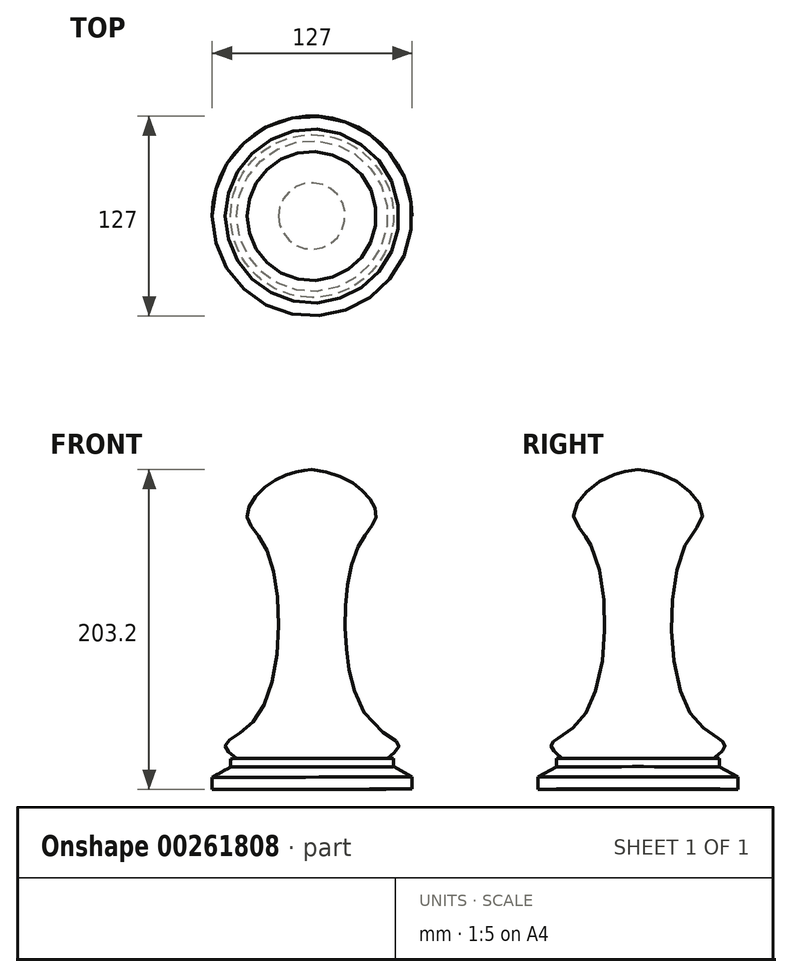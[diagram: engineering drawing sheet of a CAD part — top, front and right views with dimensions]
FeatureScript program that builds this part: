
annotation { "Feature Type Name" : "Feature", "Feature Type Description" : "" }
export const myFeature = defineFeature(function(context is Context, id is Id, definition is map)
    precondition{}
    {
        {
            var Q0;
            Q0=qCreatedBy(makeId("Front.planeOp"),FACE);
            var sketch = newSketch(context, id + "F0", { "sketchPlane" : qUnion([Q0])});
            skLineSegment(sketch, "E0", {"start": v(-0.38, 94.88) * mm, "end": v(0, -108.32) * mm, "construction": true});
            skFitSpline(sketch, "E1", {"points": [v(0, -108.32) * mm, v(-63.5, -108.32) * mm], "startDerivative": vector(-55.12, 0) * mm, "endDerivative": vector(-55.12, 0) * mm});
            skLineSegment(sketch, "E2", {"start": v(-63.5, -108.32) * mm, "end": v(-63.5, -100.64) * mm});
            skLineSegment(sketch, "E3", {"start": v(-63.5, -100.64) * mm, "end": v(-51.73, -94.04) * mm});
            skLineSegment(sketch, "E4", {"start": v(-51.73, -94.04) * mm, "end": v(-51.74, -88.77) * mm});
            skLineSegment(sketch, "E5", {"start": v(-51.74, -88.77) * mm, "end": v(-47.94, -88.76) * mm});
            skFitSpline(sketch, "E6", {"points": [v(-47.94, -88.76) * mm, v(-55.2, -80.2) * mm, v(-33.77, -60.75) * mm, v(-28.16, 42.08) * mm, v(-41.35, 65.81) * mm, v(-28.82, 84.6) * mm, v(-10.36, 93.17) * mm, v(-0.38, 94.88) * mm], "startDerivative": vector(-127.7, 97.79) * mm, "endDerivative": vector(106.56, 13.3) * mm});
            skSolve(sketch);
        }
        {
            var Q0;
            Q0=sQuery(id+"F0.wireOp",EDGE,"E1");
            var Q1;
            Q1=sQuery(id+"F0.wireOp",EDGE,"E2");
            var Q2;
            Q2=sQuery(id+"F0.wireOp",EDGE,"E3");
            var Q3;
            Q3=sQuery(id+"F0.wireOp",EDGE,"E6");
            var Q4;
            Q4=sQuery(id+"F0.wireOp",EDGE,"E4");
            var Q5;
            Q5=sQuery(id+"F0.wireOp",EDGE,"E5");
            var Q6;
            Q6=sQuery(id+"F0.wireOp",EDGE,"E0");
            revolve(context, id + "F1", {"bodyType" : ToolBodyType.SURFACE, "surfaceEntities" : qUnion([Q0, Q1, Q2, Q3, Q4, Q5]), "axis" : qUnion([Q6]), "revolveType" : RevolveType.FULL});
        }
    });
